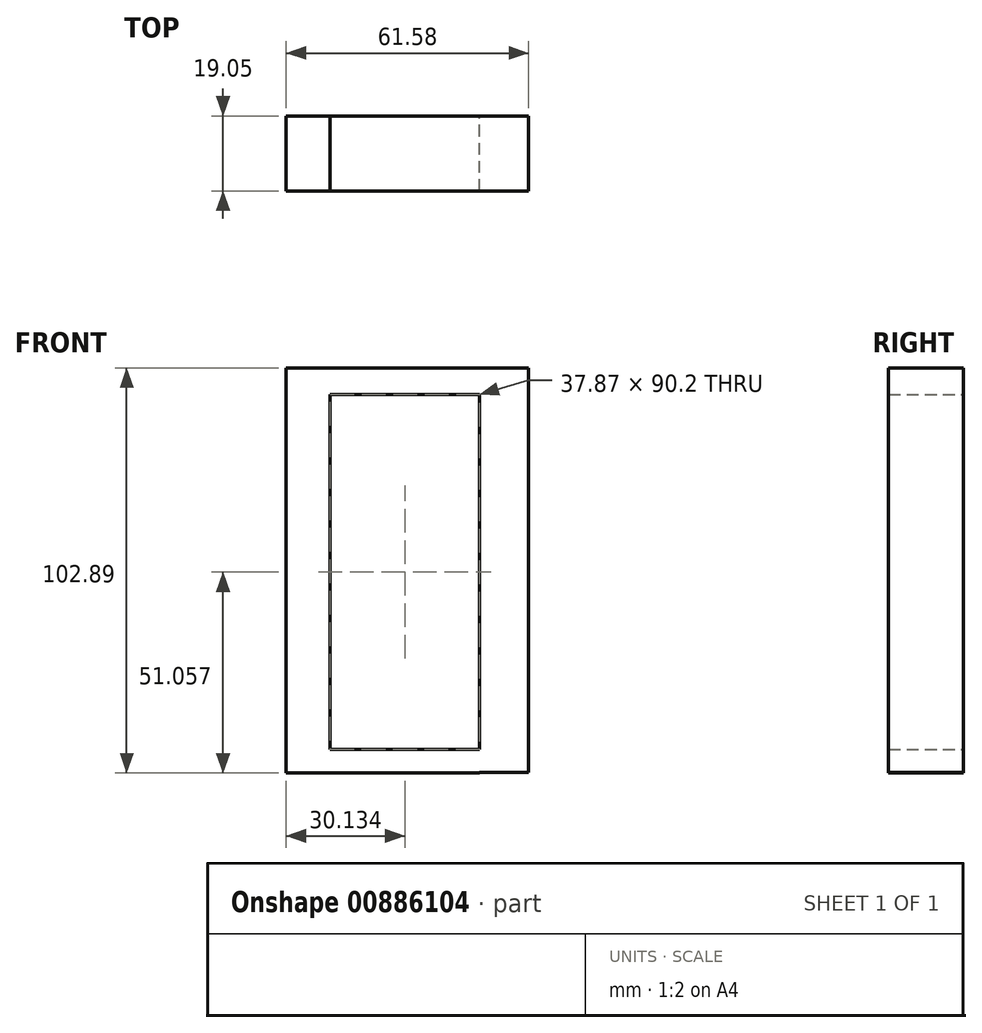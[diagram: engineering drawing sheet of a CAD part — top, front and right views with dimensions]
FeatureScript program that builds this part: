
annotation { "Feature Type Name" : "Feature", "Feature Type Description" : "" }
export const myFeature = defineFeature(function(context is Context, id is Id, definition is map)
    precondition{}
    {
        {
            var Q0;
            Q0=qCreatedBy(makeId("Front.planeOp"),FACE);
            var sketch = newSketch(context, id + "F0", { "sketchPlane" : qUnion([Q0])});
            skLineSegment(sketch, "E0.bottom", {"start": v(-70.96, 47.03) * mm, "end": v(-59.76, 47.03) * mm});
            skLineSegment(sketch, "E0.top", {"start": v(-70.96, -55.86) * mm, "end": v(-59.76, -55.86) * mm});
            skLineSegment(sketch, "E0.left", {"start": v(-70.96, 47.03) * mm, "end": v(-70.96, -55.86) * mm});
            skLineSegment(sketch, "E0.right", {"start": v(-59.76, 47.03) * mm, "end": v(-59.76, -55.86) * mm});
            skLineSegment(sketch, "E1.bottom", {"start": v(-21.9, 47.02) * mm, "end": v(-9.38, 47.02) * mm});
            skLineSegment(sketch, "E1.top", {"start": v(-21.9, -55.73) * mm, "end": v(-9.38, -55.73) * mm});
            skLineSegment(sketch, "E1.left", {"start": v(-21.9, 47.02) * mm, "end": v(-21.9, -55.73) * mm});
            skLineSegment(sketch, "E1.right", {"start": v(-9.38, 47.02) * mm, "end": v(-9.38, -55.73) * mm});
            skLineSegment(sketch, "E2.bottom", {"start": v(-59.76, 40.3) * mm, "end": v(-21.9, 40.3) * mm});
            skLineSegment(sketch, "E2.top", {"start": v(-59.76, 47.02) * mm, "end": v(-21.9, 47.02) * mm});
            skLineSegment(sketch, "E2.left", {"start": v(-59.76, 40.3) * mm, "end": v(-59.76, 47.02) * mm});
            skLineSegment(sketch, "E2.right", {"start": v(-21.9, 40.3) * mm, "end": v(-21.9, 47.02) * mm});
            skLineSegment(sketch, "E3.bottom", {"start": v(-59.76, -55.86) * mm, "end": v(-21.9, -55.86) * mm});
            skLineSegment(sketch, "E3.top", {"start": v(-59.76, -49.9) * mm, "end": v(-21.9, -49.9) * mm});
            skLineSegment(sketch, "E3.left", {"start": v(-59.76, -55.86) * mm, "end": v(-59.76, -49.9) * mm});
            skLineSegment(sketch, "E3.right", {"start": v(-21.9, -55.86) * mm, "end": v(-21.9, -49.9) * mm});
            skSolve(sketch);
        }
        {
            var Q0;
            {var subQ1=sQuery(id+"F0.wireOp",EDGE,"E0.bottom");Q0=makeQuery(id+"F0.imprint","IMPRINT",FACE,{"disambiguationData":[TD([[makeQuery(id+"F0.imprint","IMPRINT",EDGE,{"derivedFrom":subQ1}),-1.0]])]});}
            var Q1;
            Q1=makeQuery(id+"F0.imprint","IMPRINT",FACE,{"disambiguationData":[TD([[makeQuery(id+"F0.imprint","IMPRINT",EDGE,{"derivedFrom":sQuery(id+"F0.wireOp",EDGE,"E1.bottom")}),-1.0]])]});
            var Q2;
            {var subQ2=sQuery(id+"F0.wireOp",EDGE,"E3.bottom");Q2=makeQuery(id+"F0.imprint","IMPRINT",FACE,{"disambiguationData":[TD([[makeQuery(id+"F0.imprint","IMPRINT",EDGE,{"derivedFrom":subQ2}),1.0]])]});}
            var Q3;
            Q3=makeQuery(id+"F0.imprint","IMPRINT",FACE,{"disambiguationData":[TD([[makeQuery(id+"F0.imprint","IMPRINT",EDGE,{"derivedFrom":sQuery(id+"F0.wireOp",EDGE,"E2.bottom")}),1.0]])]});
            extrude(context, id + "F1", {"entities" : qUnion([Q0, Q1, Q2, Q3]), "depth" : 19.05 * mm, "offsetDistance" : 25.4 * mm});
        }
    });
